# Revit family: Vitra-İntegra-TallUnit-62014+62015+62016+62017+62018+62019
name_source: partatom
category: Furniture Systems
revit_build: Autodesk Revit 2017 (Build: 20160225_1515(x64)
units: mm (PartAtom-declared; Revit-internal decimal feet)

## family parameters
Cut with Voids When Loaded = No
Host = Face
OmniClass Number = 23.40.00.00
OmniClass Title = Equipment and Furnishings
Part Type = Normal
Room Calculation Point = No
Round Connector Dimension = Use Diameter
Shared = Yes

## types (6) — shared parameters
BIMobject category = Storage
Construction Type = Face Mounted
Default Elevation = 660 mm
Description = İntegra Tall Unit (Narrow)
Design country = Turkey
Height(mm) = 1550 mm  [stored 5.0853 ft]
IFC Classification = Furniture
Manufacturer = Vitra
Manufacturer name = Vitra
Masterformat 2014 Code = 12 35 30.23
Masterformat 2014 Description = Bathroom Casework
NBS Referans Code = 35-75-08
NBS Referans Description = Bathroom Cabinets
Nominal height = 0.000
Nominal width = 0.000
OmniClass Code = 23-31 25 13
OmniClass Description = Bathroom Cabinets
Product certification = https://vitraglobal.com
Product data url = https://www.vitraglobal.com
Product family = İntegra
Product group = Bathroom Furniture
Technical description = https://www.vitra.com.tr
Thrid Material = Vitra-AmericanValnut
UNSPSC Code = 30161801
UNSPSC Description = Bathroom Cabinets
URL = https://vitraglobal.com
Uniclass 1.4 Code = L8241
Uniclass 1.4 Description = Bathroom Cabinets
Uniclass 2.0 Code = PR-35-75-08
Uniclass 2.0 Description = Bathroom Cabinets
Uniclass 2015 Code = Pr_40_30_78_03
Uniclass 2015 Name = Bathroom Cabinets
Uniformat II Code = E2010
Uniformat II Description = Fixed Furnishings
Warranty Period (Year) = 2
Weight Net (kg) = 37,000
Youtube = https://www.youtube.com

## per-type parameters (varying)
| type | Article No. (default) | Depth(mm) | Model | Primary Material | Product SKU | Secondary Material | Width(mm) |
| TallUnit(Narrow)-Vitra-İntegra(Left)_62014 | 62014 | 250 mm | 62014 | Vitra-MattWhite | 62014 | Vitra-Bambu | 500 mm |
| TallUnit(Narrow)-Vitra-İntegra(Left)_62015 | 62015 | 360 mm | 62015 | Vitra-Kaşmir | 62015 | Vitra-MetalikCeviz | 400 mm  [stored 1.31234 ft] |
| TallUnit(Narrow)-Vitra-İntegra(Left)_62016 | 62016 | 360 mm | 62016 | Vitra-Akçaağaç | 62016 | Vitra-Kumtaşı | 400 mm  [stored 1.31234 ft] |
| TallUnit(Narrow)-Vitra-İntegra(Right)_62017 | 62017 | 360 mm | 62017 | Vitra-MattWhite | 62017 | Vitra-Bambu | 400 mm  [stored 1.31234 ft] |
| TallUnit(Narrow)-Vitra-İntegra(Right)_62018 | 62018 | 360 mm | 62018 | Vitra-Kaşmir | 62018 | Vitra-MetalikCeviz | 400 mm  [stored 1.31234 ft] |
| TallUnit(Narrow)-Vitra-İntegra(Right)_62019 | 62019 | 360 mm | 62019 | Vitra-Akçaağaç | 62019 | Vitra-Kumtaşı | 400 mm  [stored 1.31234 ft] |

note: [stored X ft] marks values corroborated as IEEE doubles in the binary element streams (Revit-internal decimal feet)

## geometry (parser evidence)
native form markers: Sweep x3
no freeform markers — native parametric forms only
